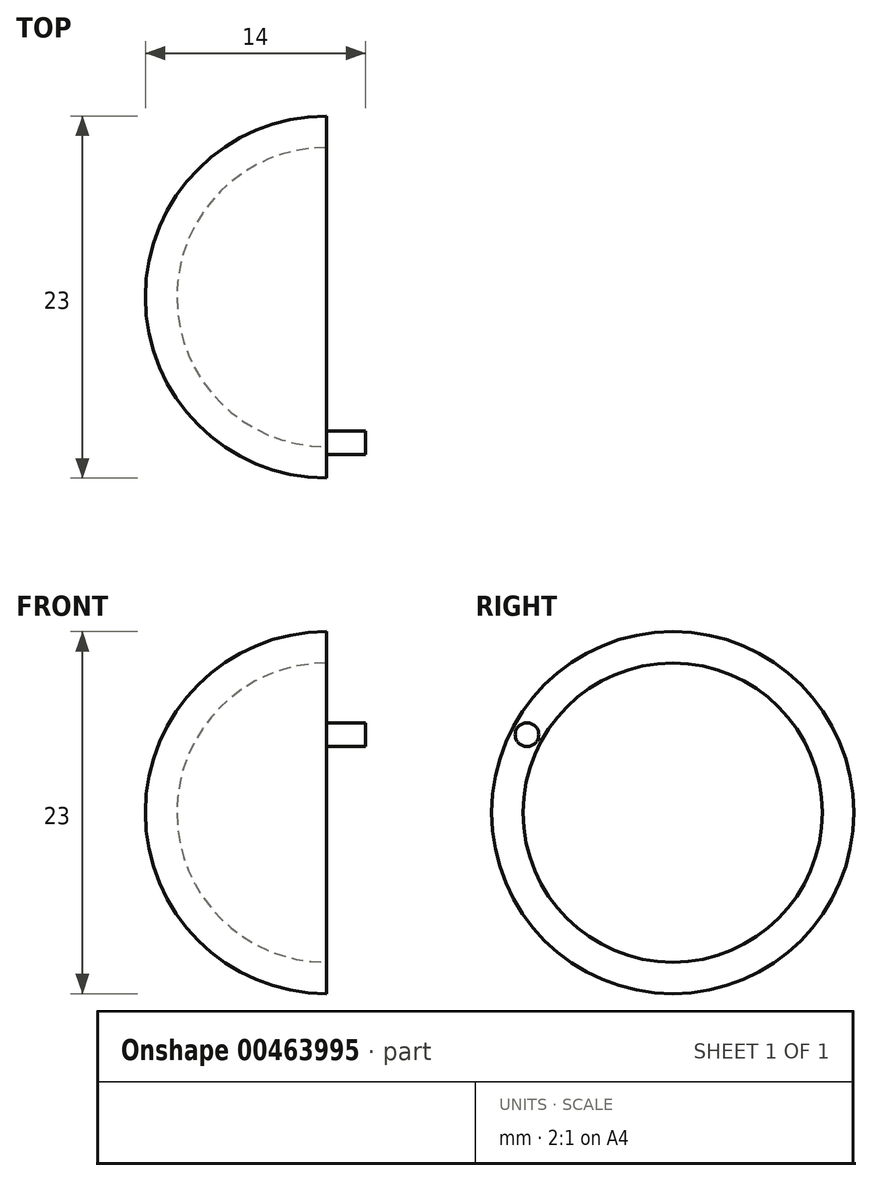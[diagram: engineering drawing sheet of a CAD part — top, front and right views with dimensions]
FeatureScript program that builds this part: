
annotation { "Feature Type Name" : "Feature", "Feature Type Description" : "" }
export const myFeature = defineFeature(function(context is Context, id is Id, definition is map)
    precondition{}
    {
        {
            var Q0;
            Q0=qCreatedBy(makeId("Top.planeOp"),FACE);
            var sketch = newSketch(context, id + "F0", { "sketchPlane" : qUnion([Q0])});
            skArc(sketch, "E0", {"start": v(0, -11.5) * mm, "mid": v(11.5, 0) * mm, "end": v(0, 11.5) * mm});
            skLineSegment(sketch, "E1", {"start": v(0, 11.5) * mm, "end": v(0, -11.5) * mm});
            skSolve(sketch);
        }
        {
            var Q0;
            Q0=makeQuery(id+"F0.imprint","IMPRINT",FACE,{"disambiguationData":[TD([[makeQuery(id+"F0.imprint","IMPRINT",EDGE,{"derivedFrom":sQuery(id+"F0.wireOp",EDGE,"E0")}),1.0]])]});
            var Q1;
            Q1=sQuery(id+"F0.wireOp",EDGE,"E1");
            revolve(context, id + "F1", {"entities" : qUnion([Q0]), "axis" : qUnion([Q1]), "revolveType" : RevolveType.FULL});
        }
        {
            var Q0;
            Q0=qCreatedBy(makeId("Top.planeOp"),FACE);
            var sketch = newSketch(context, id + "F2", { "sketchPlane" : qUnion([Q0])});
            skLineSegment(sketch, "E2.bottom", {"start": v(0, 20.33) * mm, "end": v(26.75, 20.33) * mm});
            skLineSegment(sketch, "E2.top", {"start": v(0, -20.54) * mm, "end": v(26.75, -20.54) * mm});
            skLineSegment(sketch, "E2.left", {"start": v(0, 20.33) * mm, "end": v(0, -20.54) * mm});
            skLineSegment(sketch, "E2.right", {"start": v(26.75, 20.33) * mm, "end": v(26.75, -20.54) * mm});
            skSolve(sketch);
        }
        {
            var Q0;
            Q0=qSketchRegion(id+"F2",true);
            extrude(context, id + "F3", {"entities" : qUnion([Q0]), "operationType" : NewBodyOperationType.REMOVE, "oppositeDirection" : true, "depth" : 25 * mm, "hasSecondDirection" : true, "secondDirectionOppositeDirection" : false, "secondDirectionDepth" : 37.9 * mm});
        }
        {
            var Q0;
            Q0=makeQuery(id+"F3.boolean.opBoolean","COPY",FACE,{"derivedFrom":makeQuery(id+"F3.opExtrude","SWEPT_FACE",FACE,{"disambiguationData":[OSD([sQuery(id+"F2.wireOp",EDGE,"E2.left")])]})});
            var sketch = newSketch(context, id + "F4", { "sketchPlane" : qUnion([Q0])});
            skArc(sketch, "E3", {"start": v(0, -9.5) * mm, "mid": v(9.5, 0) * mm, "end": v(0, 9.5) * mm});
            skLineSegment(sketch, "E4", {"start": v(0, 9.5) * mm, "end": v(0, -9.5) * mm});
            skSolve(sketch);
        }
        {
            var Q0;
            Q0=qSketchRegion(id+"F4",true);
            var Q1;
            Q1=sQuery(id+"F4.wireOp",EDGE,"E4");
            revolve(context, id + "F5", {"operationType" : NewBodyOperationType.REMOVE, "entities" : qUnion([Q0]), "axis" : qUnion([Q1]), "revolveType" : RevolveType.FULL, "oppositeDirection" : true});
        }
        {
            var Q0;
            Q0=makeQuery(id+"F3.boolean.opBoolean","COPY",FACE,{"derivedFrom":makeQuery(id+"F3.opExtrude","SWEPT_FACE",FACE,{"disambiguationData":[OSD([sQuery(id+"F2.wireOp",EDGE,"E2.left")])]})});
            var sketch = newSketch(context, id + "F6", { "sketchPlane" : qUnion([Q0])});
            skCircle(sketch, "E5", {"center": v(-9.26, 4.95) * mm, "radius": 0.75 * mm});
            skSolve(sketch);
        }
        {
            var Q0;
            Q0=makeQuery(id+"F6.imprint","IMPRINT",FACE,{"disambiguationData":[TD([[makeQuery(id+"F6.imprint","IMPRINT",EDGE,{"derivedFrom":sQuery(id+"F6.wireOp",EDGE,"E5")}),1.0]])]});
            extrude(context, id + "F7", {"entities" : qUnion([Q0]), "operationType" : NewBodyOperationType.ADD, "depth" : 2.5 * mm});
        }
        {
            var Q0;
            Q0=qCreatedBy(makeId("Top.planeOp"),FACE);
            cPlane(context, id + "F8", {"entities" : qUnion([Q0]), "cplaneType" : CPlaneType.OFFSET, "offset" : 11.5 * mm, "width" : 150 * mm, "height" : 150 * mm});
        }
    });
